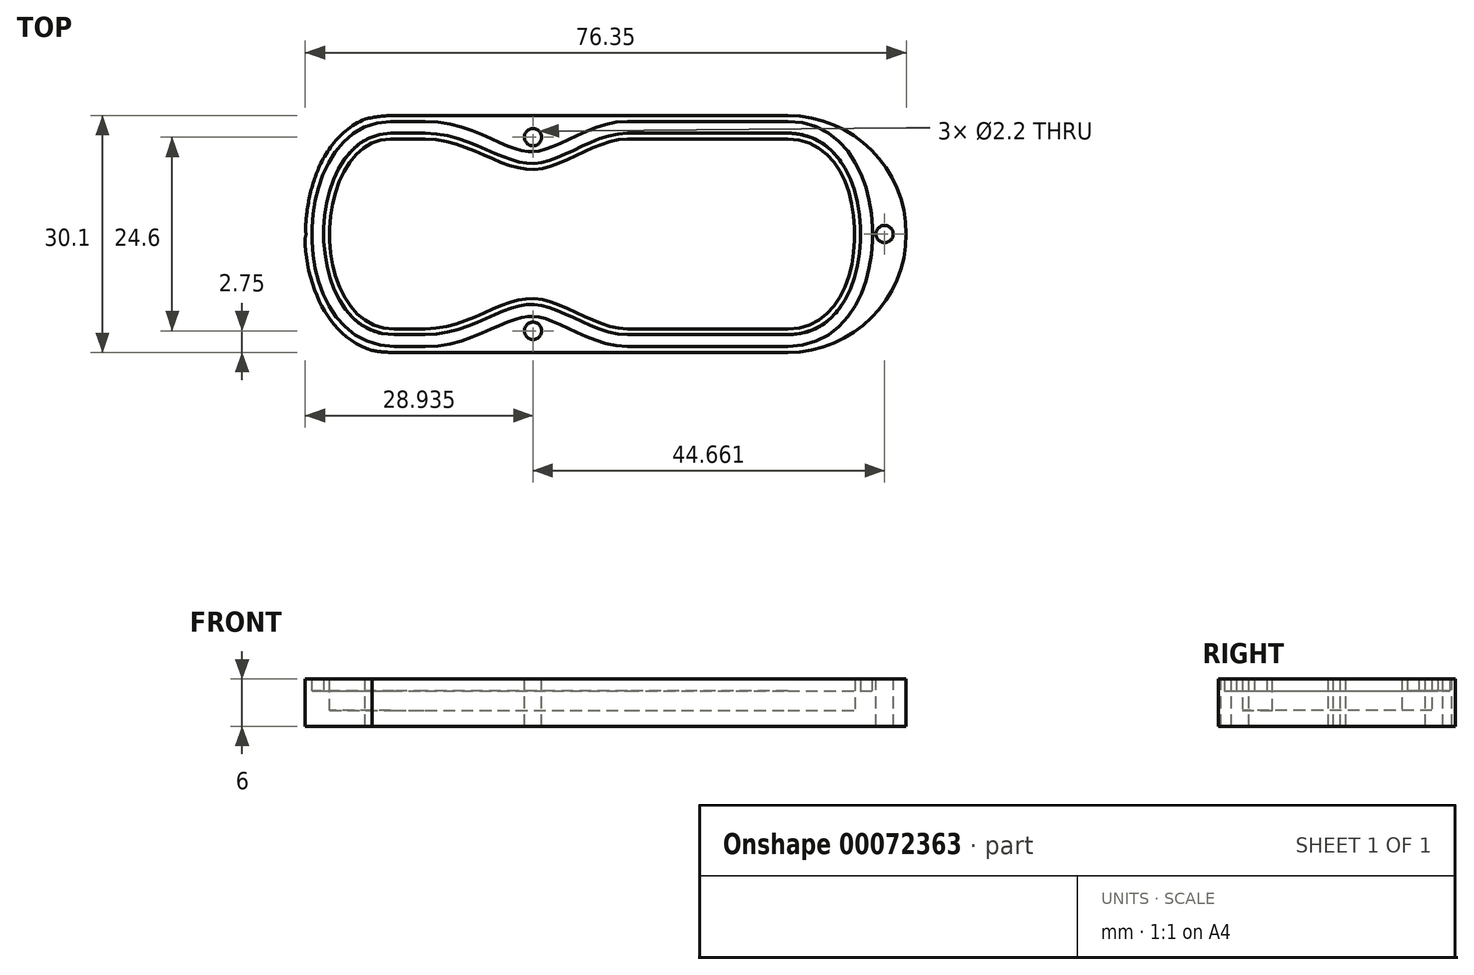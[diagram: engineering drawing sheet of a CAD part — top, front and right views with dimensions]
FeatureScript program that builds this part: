
annotation { "Feature Type Name" : "Feature", "Feature Type Description" : "" }
export const myFeature = defineFeature(function(context is Context, id is Id, definition is map)
    precondition{}
    {
        {
            var Q0;
            Q0=qCreatedBy(makeId("Top.planeOp"),FACE);
            var sketch = newSketch(context, id + "F0", { "sketchPlane" : qUnion([Q0])});
            skLineSegment(sketch, "E0.0", {"start": v(-0.21, 11.21) * mm, "end": v(-13.74, 9.64) * mm});
            skPoint(sketch, "E0.6", {"position": v(-22.82, 0.8) * mm});
            skLineSegment(sketch, "E0.9", {"start": v(-17.35, -8.55) * mm, "end": v(-6.93, -7.3) * mm});
            skLineSegment(sketch, "E0.11", {"start": v(-2.83, -7.57) * mm, "end": v(5.39, -8.81) * mm});
            skLineSegment(sketch, "E0.12", {"start": v(5.39, -8.81) * mm, "end": v(15.15, -7.7) * mm});
            skLineSegment(sketch, "E0.20", {"start": v(8.73, 7.95) * mm, "end": v(7.04, 5.13) * mm});
            skLineSegment(sketch, "E0.23", {"start": v(6.33, 4.84) * mm, "end": v(1.3, 6.86) * mm});
            skLineSegment(sketch, "E0.25", {"start": v(1.1, 7.4) * mm, "end": v(2.66, 10.02) * mm});
            skPoint(sketch, "E0.26", {"position": v(-0.21, 11.21) * mm});
            skLineSegment(sketch, "E0.28", {"start": v(-22.82, 0.8) * mm, "end": v(-22.13, -5.16) * mm});
            skCircle(sketch, "E0.39", {"center": v(-20.89, -3.72) * mm, "radius": 1 * mm});
            skCircle(sketch, "E0.40", {"center": v(9.03, 4.98) * mm, "radius": 1 * mm});
            skCircle(sketch, "E0.41", {"center": v(13.95, -6.45) * mm, "radius": 1 * mm});
            skLineSegment(sketch, "E0.42", {"start": v(13.3, -5.98) * mm, "end": v(11.51, -1.1) * mm});
            skLineSegment(sketch, "E0.43", {"start": v(8.4, -7.76) * mm, "end": v(13.3, -5.98) * mm});
            skLineSegment(sketch, "E0.44", {"start": v(6.62, -2.87) * mm, "end": v(8.4, -7.76) * mm});
            skLineSegment(sketch, "E0.45", {"start": v(11.51, -1.1) * mm, "end": v(6.62, -2.87) * mm});
            skLineSegment(sketch, "E0.46", {"start": v(-13.36, -3.82) * mm, "end": v(-15.14, 1.07) * mm});
            skLineSegment(sketch, "E0.47", {"start": v(-18.25, -5.6) * mm, "end": v(-13.36, -3.82) * mm});
            skLineSegment(sketch, "E0.48", {"start": v(-20.03, -0.7) * mm, "end": v(-18.25, -5.6) * mm});
            skLineSegment(sketch, "E0.49", {"start": v(-15.14, 1.07) * mm, "end": v(-20.03, -0.7) * mm});
            skFitSpline(sketch, "E1", {"points": [v(-13.74, 9.64) * mm, v(-22.82, 0.8) * mm], "startDerivative": vector(-9.06, -4.28) * mm, "endDerivative": vector(-11.26, -16.1) * mm});
            skFitSpline(sketch, "E2", {"points": [v(-22.13, -5.16) * mm, v(-17.35, -8.55) * mm], "startDerivative": vector(0.9, -4.16) * mm, "endDerivative": vector(8.25, 0.85) * mm});
            skFitSpline(sketch, "E3", {"points": [v(-6.93, -7.3) * mm, v(-2.83, -7.57) * mm], "startDerivative": vector(4.04, -0.71) * mm, "endDerivative": vector(4.04, -0.71) * mm});
            skFitSpline(sketch, "E4", {"points": [v(15.15, -7.7) * mm, v(17.5, -0.5) * mm, v(9.96, 8.48) * mm, v(8.73, 7.95) * mm], "startDerivative": vector(14.52, 15.53) * mm, "endDerivative": vector(-6.47, -5.85) * mm});
            skFitSpline(sketch, "E5", {"points": [v(7.04, 5.13) * mm, v(6.33, 4.84) * mm], "startDerivative": vector(-0.67, -0.7) * mm, "endDerivative": vector(-0.8, 0.41) * mm});
            skFitSpline(sketch, "E6", {"points": [v(1.3, 6.86) * mm, v(1.1, 7.4) * mm], "startDerivative": vector(-0.58, 0.33) * mm, "endDerivative": vector(0.09, 0.84) * mm});
            skFitSpline(sketch, "E7", {"points": [v(2.66, 10.02) * mm, v(-0.21, 11.21) * mm], "startDerivative": vector(0.05, 1.6) * mm, "endDerivative": vector(-2.37, 0.25) * mm});
            skLineSegment(sketch, "E8", {"start": v(-22.82, 0.8) * mm, "end": v(17.5, -0.5) * mm, "construction": true});
            skLineSegment(sketch, "E9", {"start": v(-7.54, 10.36) * mm, "end": v(-7.2, 0.3) * mm, "construction": true});
            skLineSegment(sketch, "E10", {"start": v(-7.2, 0.3) * mm, "end": v(-6.93, -7.3) * mm, "construction": true});
            skLineSegment(sketch, "E11", {"start": v(-7.2, 0.3) * mm, "end": v(38.2, 0.3) * mm, "construction": true});
            skCircle(sketch, "E12", {"center": v(0.16, 0.3) * mm, "radius": 3.84 * mm});
            skLineSegment(sketch, "E13", {"start": v(10.83, -2.4) * mm, "end": v(14.61, -1.95) * mm, "construction": true});
            skLineSegment(sketch, "E14", {"start": v(14.61, -1.95) * mm, "end": v(13.88, 4.2) * mm, "construction": true});
            skLineSegment(sketch, "E15", {"start": v(13.88, 4.2) * mm, "end": v(10.1, 3.75) * mm, "construction": true});
            skLineSegment(sketch, "E16", {"start": v(10.1, 3.75) * mm, "end": v(10.83, -2.4) * mm, "construction": true});
            skLineSegment(sketch, "E17", {"start": v(13.95, -6.45) * mm, "end": v(14.61, -6.45) * mm, "construction": true});
            skLineSegment(sketch, "E18", {"start": v(14.61, -6.45) * mm, "end": v(14.61, -1.95) * mm, "construction": true});
            skLineSegment(sketch, "E19", {"start": v(14.61, -1.95) * mm, "end": v(10.1, 3.75) * mm, "construction": true});
            skLineSegment(sketch, "E20", {"start": v(13.88, 4.2) * mm, "end": v(10.83, -2.4) * mm, "construction": true});
            skPoint(sketch, "E21", {"position": v(12.35, 0.9) * mm});
            skLineSegment(sketch, "E22", {"start": v(12.35, 0.9) * mm, "end": v(12.35, 0.3) * mm, "construction": true});
            skPoint(sketch, "E23", {"position": v(12.35, 0.3) * mm});
            skCircle(sketch, "E24", {"center": v(-35.74, 0) * mm, "radius": 12 * mm, "construction": true});
            skPoint(sketch, "E25", {"position": v(20.49, 0.3) * mm});
            skSolve(sketch);
        }
        {
            assignVariable(context, id + "F1", {"name" : "wallThickness", "anyValue" : 2});
        }
        {
            assignVariable(context, id + "F2", {"name" : "wallHeight", "anyValue" : 4});
        }
        {
            var Q0;
            Q0=qCreatedBy(makeId("Top.planeOp"),FACE);
            var sketch = newSketch(context, id + "F3", { "sketchPlane" : qUnion([Q0])});
            skCircle(sketch, "E26", {"center": v(-22.05, 12.3) * mm, "radius": 1.1 * mm});
            skCircle(sketch, "E27", {"center": v(-22.05, -12.3) * mm, "radius": 1.1 * mm});
            skCircle(sketch, "E28", {"center": v(-52, 0) * mm, "radius": 1.1 * mm});
            skCircle(sketch, "E29", {"center": v(22.6, 0) * mm, "radius": 1.1 * mm});
            skArc(sketch, "E30", {"start": v(-39.7, 15.05) * mm, "mid": v(-54.74, 0) * mm, "end": v(-39.7, -15.05) * mm});
            skArc(sketch, "E31", {"start": v(10.3, -15.05) * mm, "mid": v(25.36, 0) * mm, "end": v(10.3, 15.05) * mm});
            skLineSegment(sketch, "E32", {"start": v(-39.7, 15.05) * mm, "end": v(10.3, 15.05) * mm});
            skLineSegment(sketch, "E33", {"start": v(-39.7, -15.05) * mm, "end": v(10.3, -15.05) * mm});
            skLineSegment(sketch, "E34", {"start": v(-22.05, 24.18) * mm, "end": v(-22.05, -22.95) * mm, "construction": true});
            skCircle(sketch, "E35", {"center": v(22.6, 0) * mm, "radius": 2.75 * mm, "construction": true});
            skCircle(sketch, "E36", {"center": v(-22.05, 12.3) * mm, "radius": 2.75 * mm, "construction": true});
            skCircle(sketch, "E37", {"center": v(-22.05, -12.3) * mm, "radius": 2.75 * mm, "construction": true});
            skPoint(sketch, "E38.0", {"position": v(-35.74, 0) * mm});
            skCircle(sketch, "E39", {"center": v(-35.74, 0) * mm, "radius": 12.05 * mm, "construction": true});
            skLineSegment(sketch, "E40.0", {"start": v(-40.14, 12.05) * mm, "end": v(-35.74, 12.05) * mm});
            skLineSegment(sketch, "E40.2", {"start": v(-39.7, -12.05) * mm, "end": v(-35.74, -12.05) * mm});
            skFitSpline(sketch, "E41", {"points": [v(-40.14, 12.05) * mm, v(-47.9, 0) * mm, v(-39.7, -12.05) * mm], "startDerivative": vector(-30.13, 0) * mm, "endDerivative": vector(32.51, 0) * mm});
            skLineSegment(sketch, "E42", {"start": v(-35.74, 12.05) * mm, "end": v(-10.05, 12.05) * mm, "construction": true});
            skLineSegment(sketch, "E43", {"start": v(-35.74, -12.05) * mm, "end": v(-10.05, -12.05) * mm, "construction": true});
            skFitSpline(sketch, "E44", {"points": [v(-35.74, 12.05) * mm, v(-22.05, 8.2) * mm, v(-10.05, 12.05) * mm], "startDerivative": vector(32.18, 0) * mm, "endDerivative": vector(25.65, 0) * mm});
            skFitSpline(sketch, "E45", {"points": [v(-35.74, -12.05) * mm, v(-22.05, -8.2) * mm, v(-10.05, -12.05) * mm], "startDerivative": vector(32.18, 0) * mm, "endDerivative": vector(25.65, 0) * mm});
            skLineSegment(sketch, "E46", {"start": v(-10.05, 12.05) * mm, "end": v(0, 12.05) * mm});
            skLineSegment(sketch, "E47", {"start": v(-10.05, -12.05) * mm, "end": v(10.3, -12.05) * mm});
            skFitSpline(sketch, "E48", {"points": [v(10.3, 12.05) * mm, v(18.81, 0) * mm, v(10.3, -12.05) * mm], "startDerivative": vector(35.04, 0) * mm, "endDerivative": vector(-35.32, 0) * mm});
            skLineSegment(sketch, "E49", {"start": v(0, 12.05) * mm, "end": v(10.3, 12.05) * mm});
            skLineSegment(sketch, "E50", {"start": v(-52, 0) * mm, "end": v(-50.37, 2.22) * mm, "construction": true});
            skLineSegment(sketch, "E51", {"start": v(-50.37, 2.22) * mm, "end": v(-50.37, -2.22) * mm, "construction": true});
            skLineSegment(sketch, "E52", {"start": v(-50.37, -2.22) * mm, "end": v(-52, 0) * mm, "construction": true});
            skLineSegment(sketch, "E53", {"start": v(-52.46, 2.71) * mm, "end": v(-52.46, -2.71) * mm});
            skFitSpline(sketch, "E54.0", {"points": [v(-40.14, 15.05) * mm, v(-41.07, 15.05) * mm, v(-42.9, 14.76) * mm, v(-45.25, 13.56) * mm, v(-47.13, 11.83) * mm, v(-48.56, 9.78) * mm, v(-49.62, 7.5) * mm, v(-50.36, 5.07) * mm, v(-50.8, 2.52) * mm, v(-51, -0.95) * mm, v(-50.6, -4.41) * mm, v(-49.56, -7.66) * mm, v(-48.45, -9.93) * mm, v(-46.93, -11.96) * mm, v(-44.95, -13.65) * mm, v(-42.5, -14.78) * mm, v(-40.65, -15.05) * mm, v(-39.7, -15.05) * mm], "construction": true});
            skArc(sketch, "E55", {"start": v(-48.87, 9.06) * mm, "mid": v(-51.17, 6.17) * mm, "end": v(-52.46, 2.71) * mm});
            skFitSpline(sketch, "E56", {"points": [v(-40.14, 15.05) * mm, v(-41.07, 15.05) * mm, v(-42.9, 14.76) * mm, v(-45.25, 13.56) * mm, v(-47.13, 11.83) * mm, v(-48.56, 9.78) * mm, v(-49.62, 7.5) * mm, v(-50.36, 5.07) * mm, v(-50.8, 2.52) * mm, v(-51, -0.95) * mm, v(-50.6, -4.41) * mm, v(-49.56, -7.66) * mm, v(-48.45, -9.93) * mm, v(-46.93, -11.96) * mm, v(-44.95, -13.65) * mm, v(-42.5, -14.78) * mm, v(-40.65, -15.05) * mm, v(-39.7, -15.05) * mm]});
            skFitSpline(sketch, "E57", {"points": [v(-40.14, 15.05) * mm, v(-41.07, 15.05) * mm, v(-42.9, 14.76) * mm, v(-45.25, 13.56) * mm, v(-47.13, 11.83) * mm, v(-48.56, 9.78) * mm, v(-49.62, 7.5) * mm, v(-50.36, 5.07) * mm, v(-50.8, 2.52) * mm, v(-51, -0.95) * mm, v(-50.6, -4.41) * mm, v(-49.56, -7.66) * mm, v(-48.45, -9.93) * mm, v(-46.93, -11.96) * mm, v(-44.95, -13.65) * mm, v(-42.5, -14.78) * mm, v(-40.65, -15.05) * mm, v(-39.7, -15.05) * mm], "construction": true});
            skArc(sketch, "E58", {"start": v(-52.46, 2.71) * mm, "mid": v(-52.4, -2.72) * mm, "end": v(-50.76, 2.46) * mm, "construction": true});
            skArc(sketch, "E59", {"start": v(-50.76, 2.46) * mm, "mid": v(-51.59, 2.72) * mm, "end": v(-52.46, 2.71) * mm});
            skSolve(sketch);
        }
        {
            var Q0;
            Q0=makeQuery(id+"F3.imprint","IMPRINT",FACE,{"disambiguationData":[TD([[makeQuery(id+"F3.imprint","IMPRINT",EDGE,{"derivedFrom":sQuery(id+"F3.wireOp",EDGE,"E26")}),-1.0]])]});
            var Q1;
            Q1=makeQuery(id+"F3.imprint","IMPRINT",FACE,{"disambiguationData":[TD([[makeQuery(id+"F3.imprint","IMPRINT",EDGE,{"derivedFrom":sQuery(id+"F3.wireOp",EDGE,"E40.0")}),-1.0]])]});
            extrude(context, id + "F4", {"entities" : qUnion([Q0, Q1]), "oppositeDirection" : true, "depth" : (getVariable(context, 'wallThickness')) * mm});
        }
        {
            var Q0;
            Q0=makeQuery(id+"F3.imprint","IMPRINT",FACE,{"disambiguationData":[TD([[makeQuery(id+"F3.imprint","IMPRINT",EDGE,{"derivedFrom":sQuery(id+"F3.wireOp",EDGE,"E26")}),-1.0]])]});
            extrude(context, id + "F5", {"entities" : qUnion([Q0]), "operationType" : NewBodyOperationType.ADD, "depth" : (getVariable(context, 'wallHeight')) * mm});
        }
        {
            var Q0;
            Q0=qCreatedBy(makeId("Right.planeOp"),FACE);
            var sketch = newSketch(context, id + "F6", { "sketchPlane" : qUnion([Q0])});
            skPoint(sketch, "E60.0", {"position": v(12.05, 0) * mm});
            skLineSegment(sketch, "E61", {"start": v(12.05, 0) * mm, "end": v(12.05, 4) * mm, "construction": true});
            skLineSegment(sketch, "E62.bottom", {"start": v(14.3, 4) * mm, "end": v(12.8, 4) * mm});
            skLineSegment(sketch, "E62.top", {"start": v(14.3, 2.5) * mm, "end": v(12.8, 2.5) * mm});
            skLineSegment(sketch, "E62.left", {"start": v(14.3, 4) * mm, "end": v(14.3, 2.5) * mm});
            skLineSegment(sketch, "E62.right", {"start": v(12.8, 4) * mm, "end": v(12.8, 2.5) * mm});
            skSolve(sketch);
        }
        {
            var Q0;
            Q0=makeQuery(id+"F6.imprint","IMPRINT",FACE,{"disambiguationData":[TD([[makeQuery(id+"F6.imprint","IMPRINT",EDGE,{"derivedFrom":sQuery(id+"F6.wireOp",EDGE,"E62.bottom")}),1.0]])]});
            var Q1;
            Q1=sQuery(id+"F3.wireOp",EDGE,"E46");
            var Q2;
            Q2=sQuery(id+"F3.wireOp",EDGE,"E44");
            var Q3;
            Q3=sQuery(id+"F3.wireOp",EDGE,"E40.0");
            var Q4;
            Q4=sQuery(id+"F3.wireOp",EDGE,"E41");
            var Q5;
            Q5=sQuery(id+"F3.wireOp",EDGE,"E40.2");
            var Q6;
            Q6=sQuery(id+"F3.wireOp",EDGE,"E45");
            var Q7;
            Q7=sQuery(id+"F3.wireOp",EDGE,"E47");
            var Q8;
            Q8=sQuery(id+"F3.wireOp",EDGE,"E48");
            var Q9;
            Q9=sQuery(id+"F3.wireOp",EDGE,"E49");
            sweep(context, id + "F7", {"operationType" : NewBodyOperationType.REMOVE, "profiles" : qUnion([Q0]), "path" : qUnion([Q1, Q2, Q3, Q4, Q5, Q6, Q7, Q8, Q9])});
        }
    });
